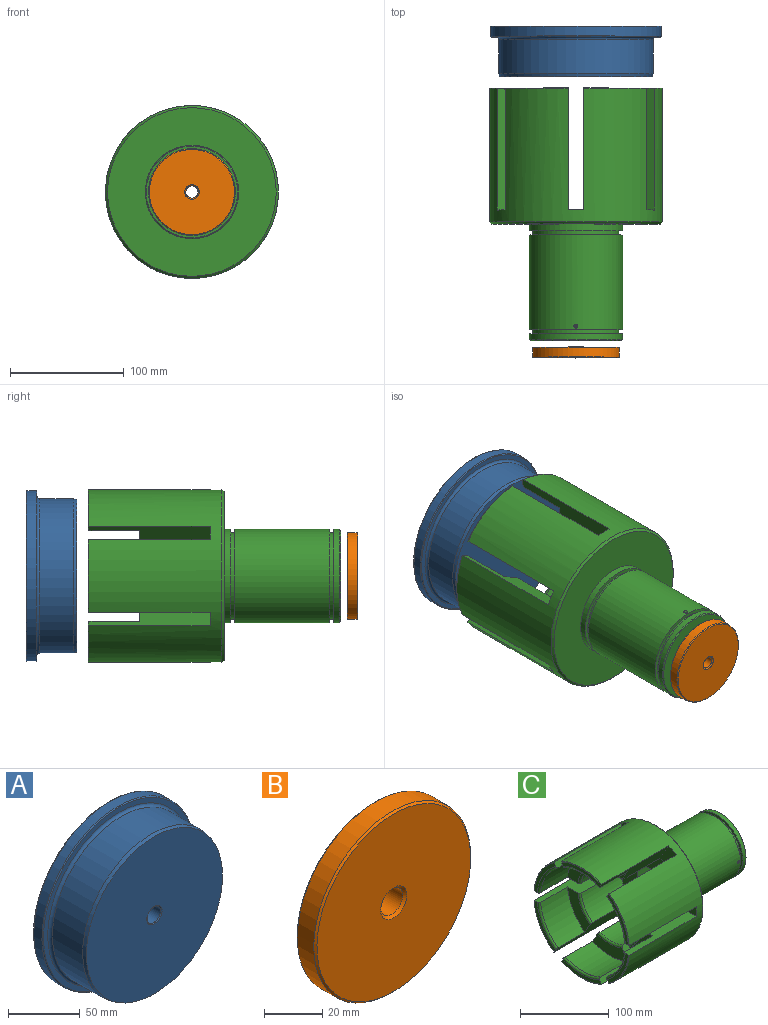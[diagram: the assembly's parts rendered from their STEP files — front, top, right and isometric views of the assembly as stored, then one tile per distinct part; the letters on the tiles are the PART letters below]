
ASSEMBLY  parts=3 mates=2
PART A: 12 faces, bbox 162.2x44.5x162.2 mm
  f0: torus R=69.98mm, axis (0,1,0), area 1546mm2, adj f1,f11
  f1: cylinder r=67.69mm len=135.38mm, axis (0,1,0), area 12672.3mm2, adj f0,f2
  f2: cone r=66.93mm half-angle=15deg, axis (0,1,0), area 1245.1mm2, adj f1,f3
  f3: plane 133.86x133.86mm, normal (0,-1,0), area 13895.8mm2, adj f2,f4
  f4: torus R=7.51mm, axis (0,1,0), area 52.8mm2, adj f3,f5
  f5: cylinder r=6.74mm len=42.93mm, axis (0,1,0), area 1818.9mm2, adj f4,f6
  f6: torus R=7.51mm, axis (0,1,0), area 52.8mm2, adj f5,f7
  f7: plane 148.34x148.34mm, normal (0,1,0), area 17104.6mm2, adj f6,f8
  f8: torus R=74.17mm, axis (0,1,0), area 561.4mm2, adj f7,f9
  f9: cylinder r=74.93mm len=149.86mm, axis (0,1,0), area 3766.9mm2, adj f8,f10
  f10: torus R=74.17mm, axis (0,1,0), area 561.4mm2, adj f9,f11
  f11: plane 148.34x148.34mm, normal (0,-1,0), area 1897.9mm2, adj f0,f10
PART B: 8 faces, bbox 76.2x9.5x76.2 mm
  f0: cylinder r=5.36mm len=10.72mm, axis (0,1,0), area 252.2mm2, adj f6,f7
  f1: cylinder r=38.1mm len=76.2mm, axis (0,1,0), area 1915.4mm2, adj f4,f5
  f2: plane 74.68x74.68mm, normal (0,-1,0), area 4252.1mm2, adj f4,f6
  f3: plane 74.68x74.68mm, normal (0,1,0), area 4252.1mm2, adj f5,f7
  f4: cone r=37.34mm half-angle=45deg, axis (0,1,0), area 255.4mm2, adj f1,f2
  f5: cone r=38.1mm half-angle=45deg, axis (0,-1,0), area 255.4mm2, adj f1,f3
  f6: cone r=5.36mm half-angle=45deg, axis (0,-1,0), area 53mm2, adj f0,f2
  f7: cone r=6.37mm half-angle=45deg, axis (0,1,0), area 53mm2, adj f0,f3
PART C: 83 faces, bbox 230.2x172.1x172.8 mm
  f0: cylinder r=40.96mm len=82.96mm, axis (1,0,0), area 21329.9mm2, adj f1,f2,f3,f4
  f1: plane 81.92x81.92mm, normal (1,0,0), area 770.3mm2, adj f0,f5
  f2: plane 81.92x81.92mm, normal (-1,0,0), area 770.3mm2, adj f0,f6
  f3: bspline ~3.43x3.43mm, area 15.5mm2, adj f0,f7
  f4: bspline ~2.62x2.1mm, area 0mm2, adj f0
  f5: cylinder r=37.85mm len=75.69mm, axis (1,0,0), area 924.1mm2, adj f1,f8
  f6: cylinder r=37.85mm len=75.69mm, axis (1,0,0), area 924.1mm2, adj f2,f9
  f7: plane 0.89x0.89mm, normal (0,-1,0), area 0.6mm2, adj f3
  f8: plane 81.92x81.92mm, normal (-1,0,0), area 770.3mm2, adj f5,f10
  f9: plane 81.92x81.92mm, normal (1,0,0), area 770.3mm2, adj f6,f11
  f10: cylinder r=40.96mm len=81.92mm, axis (1,0,0), area 1326.9mm2, adj f8,f12
  f11: cylinder r=40.96mm len=81.92mm, axis (1,0,0), area 1470.7mm2, adj f9,f13
  f12: cone r=40.2mm half-angle=45deg, axis (-1,0,0), area 274.7mm2, adj f10,f14
  f13: plane 147.92x147.92mm, normal (1,0,0), area 11914mm2, adj f11,f15
  f14: plane 80.39x80.39mm, normal (1,0,0), area 3262.1mm2, adj f12,f16,f17,f18,f19,f20,f21,f22
  f15: cone r=73.96mm half-angle=45deg, axis (-1,0,0), area 1285.2mm2, adj f13,f24
  f16: plane 120.4x48.84mm, normal (0,1,0), area 4471.9mm2, adj f14,f17,f21,f23,f25
  f17: plane 120.4x48.84mm, normal (0,0,-1), area 4471.9mm2, adj f14,f16,f18,f19,f25
  f18: cone r=23.18mm half-angle=45deg, axis (1,0,0), area 0mm2, adj f14,f17
  f19: plane 120.4x48.84mm, normal (0,-1,0), area 4471.9mm2, adj f14,f17,f20,f21,f25
  f20: cone r=23.18mm half-angle=45deg, axis (1,0,0), area 0mm2, adj f14,f19
  f21: plane 120.4x48.84mm, normal (0,0,1), area 4471.9mm2, adj f14,f16,f19,f22,f25
  f22: cone r=23.18mm half-angle=45deg, axis (1,0,0), area 0mm2, adj f14,f21
  f23: cone r=23.18mm half-angle=45deg, axis (1,0,0), area 0mm2, adj f14,f16
  f24: cylinder r=75.89mm len=151.78mm, axis (1,0,0), area 46978.8mm2, adj f15,f26,f27,f28,f29,f30,f31,f32
  f25: plane 97.6x97.6mm, normal (-1,0,0), area 5852.5mm2, adj f16,f17,f19,f21,f50
  f26: plane 107.15x23.75mm, normal (0,-0.87,0.5), area 2044mm2, adj f24,f27,f49,f50,f51,f52,f53,f54
  f27: torus R=75.25mm, axis (1,0,0), area 65.4mm2, adj f24,f26,f28,f51
  f28: plane 107.15x23.75mm, normal (0,0.87,0.5), area 2044mm2, adj f24,f27,f29,f50,f51,f52,f53,f54
  f29: plane 30.4x25.4mm, normal (-1,0,0), area 368.9mm2, adj f24,f28,f30,f50
  f30: plane 107.15x23.75mm, normal (0,-0.87,-0.5), area 2044mm2, adj f24,f29,f31,f50,f56,f57,f58,f59
  f31: torus R=75.25mm, axis (1,0,0), area 65.4mm2, adj f24,f30,f32,f60
  f32: plane 107.15x27.4mm, normal (0,0,1), area 2044mm2, adj f24,f31,f33,f50,f56,f57,f58,f59
  f33: plane 27.56x13.59mm, normal (-1,0,0), area 368.9mm2, adj f24,f32,f34,f50
  f34: plane 107.15x27.4mm, normal (0,0,-1), area 2044mm2, adj f24,f33,f35,f50,f61,f62,f63,f64
  f35: torus R=75.25mm, axis (1,0,0), area 65.4mm2, adj f24,f34,f36,f61
  f36: plane 107.15x23.75mm, normal (0,-0.87,0.5), area 2044mm2, adj f24,f35,f37,f50,f61,f62,f63,f64
  f37: plane 30.4x25.4mm, normal (-1,0,0), area 368.9mm2, adj f24,f36,f38,f50
  f38: plane 107.15x23.75mm, normal (0,0.87,-0.5), area 2044mm2, adj f24,f37,f39,f50,f66,f67,f68,f69
  f39: torus R=75.25mm, axis (1,0,0), area 65.4mm2, adj f24,f38,f40,f66
  f40: plane 107.15x23.75mm, normal (0,-0.87,-0.5), area 2044mm2, adj f24,f39,f41,f50,f66,f67,f68,f69
  f41: plane 30.4x25.4mm, normal (-1,0,0), area 368.9mm2, adj f24,f40,f42,f50
  f42: plane 107.15x23.75mm, normal (0,0.87,0.5), area 2044mm2, adj f24,f41,f43,f50,f71,f72,f73,f74
  f43: torus R=75.25mm, axis (1,0,0), area 65.4mm2, adj f24,f42,f44,f75
  f44: plane 107.15x27.4mm, normal (0,0,-1), area 2044mm2, adj f24,f43,f45,f50,f71,f72,f73,f74
  f45: plane 27.56x13.59mm, normal (-1,0,0), area 368.9mm2, adj f24,f44,f46,f50
  f46: plane 107.15x27.4mm, normal (0,0,1), area 2044mm2, adj f24,f45,f47,f50,f76,f77,f78,f79
  f47: torus R=75.25mm, axis (1,0,0), area 65.4mm2, adj f24,f46,f48,f76
  f48: plane 107.15x23.75mm, normal (0,0.87,-0.5), area 2044mm2, adj f24,f47,f49,f50,f76,f77,f78,f79
  f49: plane 30.4x25.4mm, normal (-1,0,0), area 368.9mm2, adj f24,f26,f48,f50
  f50: cylinder r=48.8mm len=97.6mm, axis (1,0,0), area 14106.3mm2, adj f25,f26,f28,f29,f30,f32,f33,f34
  f51: plane 63.18x11.22mm, normal (-1,0,0), area 307.4mm2, adj f26,f27,f28,f52
  f52: torus R=70.35mm, axis (1,0,0), area 233.1mm2, adj f26,f28,f51,f53
  f53: cylinder r=67.81mm len=55.7mm, axis (1,0,0), area 2463.7mm2, adj f26,f28,f52,f54
  f54: plane 55.7x20.34mm, normal (-1,0,0), area 802.9mm2, adj f26,f28,f53,f55
  f55: torus R=51.34mm, axis (1,0,0), area 153.7mm2, adj f26,f28,f50,f54
  f56: torus R=51.34mm, axis (1,0,0), area 153.7mm2, adj f30,f32,f50,f57
  f57: plane 48.23x36.14mm, normal (-1,0,0), area 802.9mm2, adj f30,f32,f56,f58
  f58: cylinder r=67.81mm len=48.23mm, axis (1,0,0), area 2463.7mm2, adj f30,f32,f57,f59
  f59: torus R=70.35mm, axis (1,0,0), area 233.1mm2, adj f30,f32,f58,f60
  f60: plane 54.71x34.05mm, normal (-1,0,0), area 307.4mm2, adj f30,f31,f32,f59
  f61: plane 54.71x34.05mm, normal (-1,0,0), area 307.4mm2, adj f34,f35,f36,f62
  f62: torus R=70.35mm, axis (1,0,0), area 233.1mm2, adj f34,f36,f61,f63
  f63: cylinder r=67.81mm len=48.23mm, axis (1,0,0), area 2463.7mm2, adj f34,f36,f62,f64
  f64: plane 48.23x36.14mm, normal (-1,0,0), area 802.9mm2, adj f34,f36,f63,f65
  f65: torus R=51.34mm, axis (1,0,0), area 153.7mm2, adj f34,f36,f50,f64
  f66: plane 63.18x11.22mm, normal (-1,0,0), area 307.4mm2, adj f38,f39,f40,f67
  f67: torus R=70.35mm, axis (1,0,0), area 233.1mm2, adj f38,f40,f66,f68
  f68: cylinder r=67.81mm len=55.7mm, axis (1,0,0), area 2463.7mm2, adj f38,f40,f67,f69
  f69: plane 55.7x20.34mm, normal (-1,0,0), area 802.9mm2, adj f38,f40,f68,f70
  f70: torus R=51.34mm, axis (1,0,0), area 153.7mm2, adj f38,f40,f50,f69
  f71: torus R=51.34mm, axis (1,0,0), area 153.7mm2, adj f42,f44,f50,f72
  f72: plane 48.23x36.14mm, normal (-1,0,0), area 802.9mm2, adj f42,f44,f71,f73
  f73: cylinder r=67.81mm len=48.23mm, axis (1,0,0), area 2463.7mm2, adj f42,f44,f72,f74
  f74: torus R=70.35mm, axis (1,0,0), area 233.1mm2, adj f42,f44,f73,f75
  f75: plane 54.71x34.05mm, normal (-1,0,0), area 307.4mm2, adj f42,f43,f44,f74
  f76: plane 54.71x34.05mm, normal (-1,0,0), area 307.4mm2, adj f46,f47,f48,f77
  f77: torus R=70.35mm, axis (1,0,0), area 233.1mm2, adj f46,f48,f76,f78
  f78: cylinder r=67.81mm len=48.23mm, axis (1,0,0), area 2463.7mm2, adj f46,f48,f77,f79
  f79: plane 48.23x36.14mm, normal (-1,0,0), area 802.9mm2, adj f46,f48,f78,f80
  f80: torus R=51.34mm, axis (1,0,0), area 153.7mm2, adj f46,f48,f50,f79
  f81: plane 1.29x1.29mm, normal (0,-1,0), area 0.6mm2, adj f82
  f82: bspline ~0.9x0.89mm, area 0mm2, adj f81
PLACE A t=(63.35,127.47,-64.09)mm
PLACE B t=(63.35,-154.19,-64.09)mm
PLACE C rot(axis=(-0.58,0.58,-0.58),120deg) t=(63.35,-46.24,-64.09)mm
MATE cylindrical B.f1 <-> C.f0  axis (0,1,0) through (63.35,-158.95,-64.09)mm
MATE cylindrical C.f0 <-> A.f0  axis (0,-1,0) through (63.35,49.06,-64.09)mm
